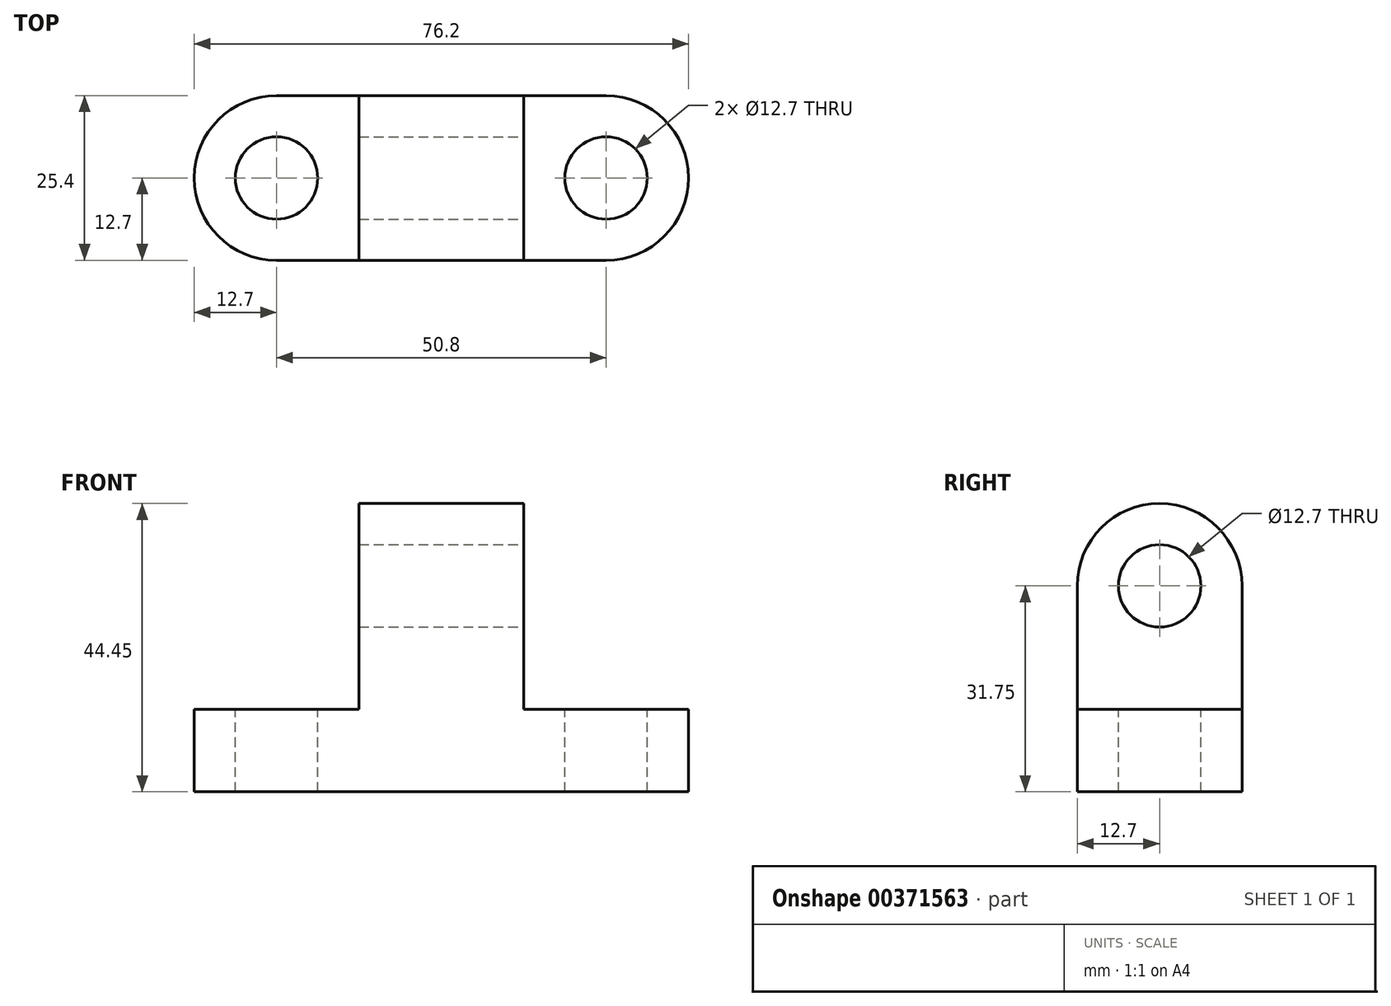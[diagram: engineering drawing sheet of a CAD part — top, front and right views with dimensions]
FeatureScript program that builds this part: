
annotation { "Feature Type Name" : "Feature", "Feature Type Description" : "" }
export const myFeature = defineFeature(function(context is Context, id is Id, definition is map)
    precondition{}
    {
        {
            var Q0;
            Q0=qCreatedBy(makeId("Front.planeOp"),FACE);
            var sketch = newSketch(context, id + "F0", { "sketchPlane" : qUnion([Q0])});
            skLineSegment(sketch, "E0", {"start": v(0, 0) * mm, "end": v(76.2, 0) * mm});
            skLineSegment(sketch, "E1", {"start": v(76.2, 0) * mm, "end": v(76.2, 12.7) * mm});
            skLineSegment(sketch, "E2", {"start": v(76.2, 12.7) * mm, "end": v(50.8, 12.7) * mm});
            skLineSegment(sketch, "E3", {"start": v(50.8, 12.7) * mm, "end": v(50.8, 44.45) * mm});
            skLineSegment(sketch, "E4", {"start": v(50.8, 44.45) * mm, "end": v(25.4, 44.45) * mm});
            skLineSegment(sketch, "E5", {"start": v(25.4, 44.45) * mm, "end": v(25.4, 12.7) * mm});
            skLineSegment(sketch, "E6", {"start": v(25.4, 12.7) * mm, "end": v(0, 12.7) * mm});
            skLineSegment(sketch, "E7", {"start": v(0, 12.7) * mm, "end": v(0, 0) * mm});
            skSolve(sketch);
        }
        {
            var Q0;
            Q0=makeQuery(id+"F0.imprint","IMPRINT",FACE,{"disambiguationData":[TD([[makeQuery(id+"F0.imprint","IMPRINT",EDGE,{"derivedFrom":sQuery(id+"F0.wireOp",EDGE,"E0")}),1.0]])]});
            extrude(context, id + "F1", {"entities" : qUnion([Q0]), "depth" : 25.4 * mm});
        }
        {
            var Q0;
            Q0=makeQuery(id+"F1.opExtrude","SWEPT_FACE",FACE,{"disambiguationData":[OSD([sQuery(id+"F0.wireOp",EDGE,"E3")])]});
            var sketch = newSketch(context, id + "F2", { "sketchPlane" : qUnion([Q0])});
            skCircle(sketch, "E8", {"center": v(-12.7, 31.75) * mm, "radius": 6.35 * mm});
            skPoint(sketch, "E8.centerSnap0", {"position": v(-12.7, 44.45) * mm});
            skArc(sketch, "E9", {"start": v(0, 31.75) * mm, "mid": v(-12.7, 44.45) * mm, "end": v(-25.4, 31.75) * mm});
            skSolve(sketch);
        }
        {
            var Q0;
            {var subQ0=sQuery(id+"F2.wireOp",EDGE,"E9");var subQ1=sQuery(id+"F0.wireOp",EDGE,"E3");var subQ2=makeQuery(id+"F1.opExtrude","CAP_EDGE",EDGE,{"disambiguationData":[OSD([subQ1])],"isStart":false});var subQ3=makeQuery(id+"F2.imprint","INTERSECT",VERTEX,{"derivedFrom":[subQ2,subQ0]});Q0=makeQuery(id+"F2.imprint","IMPRINT",FACE,{"disambiguationData":[TD([[makeQuery(id+"F2.imprint","IMPRINT",EDGE,{"disambiguationData":[TD([[subQ3,1.0]])],"derivedFrom":subQ0}),-1.0]])]});}
            var Q1;
            {var subQ0=sQuery(id+"F2.wireOp",EDGE,"E9");var subQ1=sQuery(id+"F0.wireOp",EDGE,"E3");var subQ2=makeQuery(id+"F1.opExtrude","CAP_EDGE",EDGE,{"disambiguationData":[OSD([subQ1])],"isStart":true});var subQ3=makeQuery(id+"F2.imprint","INTERSECT",VERTEX,{"derivedFrom":[subQ2,subQ0]});Q1=makeQuery(id+"F2.imprint","IMPRINT",FACE,{"disambiguationData":[TD([[makeQuery(id+"F2.imprint","IMPRINT",EDGE,{"disambiguationData":[TD([[subQ3,-1.0]])],"derivedFrom":subQ0}),-1.0]])]});}
            var Q2;
            Q2=makeQuery(id+"F2.imprint","IMPRINT",FACE,{"disambiguationData":[TD([[makeQuery(id+"F2.imprint","IMPRINT",EDGE,{"derivedFrom":sQuery(id+"F2.wireOp",EDGE,"E8")}),1.0]])]});
            extrude(context, id + "F3", {"entities" : qUnion([Q0, Q1, Q2]), "operationType" : NewBodyOperationType.REMOVE, "oppositeDirection" : true, "depth" : 25.4 * mm});
        }
        {
            var Q0;
            Q0=makeQuery(id+"F1.opExtrude","SWEPT_FACE",FACE,{"disambiguationData":[OSD([sQuery(id+"F0.wireOp",EDGE,"E6")])]});
            var sketch = newSketch(context, id + "F4", { "sketchPlane" : qUnion([Q0])});
            skCircle(sketch, "E10", {"center": v(12.7, -12.7) * mm, "radius": 6.35 * mm});
            skPoint(sketch, "E10.centerSnap0", {"position": v(0, -12.7) * mm});
            skArc(sketch, "E11", {"start": v(12.7, 0) * mm, "mid": v(0, -12.7) * mm, "end": v(12.7, -25.4) * mm});
            skSolve(sketch);
        }
        {
            var Q0;
            {var subQ0=sQuery(id+"F4.wireOp",EDGE,"E11");var subQ1=sQuery(id+"F0.wireOp",EDGE,"E6");var subQ2=makeQuery(id+"F1.opExtrude","CAP_EDGE",EDGE,{"disambiguationData":[OSD([subQ1])],"isStart":true});var subQ3=makeQuery(id+"F4.imprint","INTERSECT",VERTEX,{"derivedFrom":[subQ2,subQ0]});Q0=makeQuery(id+"F4.imprint","IMPRINT",FACE,{"disambiguationData":[TD([[makeQuery(id+"F4.imprint","IMPRINT",EDGE,{"disambiguationData":[TD([[subQ3,-1.0]])],"derivedFrom":subQ0}),-1.0]])]});}
            var Q1;
            Q1=makeQuery(id+"F4.imprint","IMPRINT",FACE,{"disambiguationData":[TD([[makeQuery(id+"F4.imprint","IMPRINT",EDGE,{"derivedFrom":sQuery(id+"F4.wireOp",EDGE,"E10")}),1.0]])]});
            var Q2;
            {var subQ0=sQuery(id+"F4.wireOp",EDGE,"E11");var subQ1=sQuery(id+"F0.wireOp",EDGE,"E6");var subQ2=makeQuery(id+"F1.opExtrude","CAP_EDGE",EDGE,{"disambiguationData":[OSD([subQ1])],"isStart":false});var subQ3=makeQuery(id+"F4.imprint","INTERSECT",VERTEX,{"derivedFrom":[subQ2,subQ0]});Q2=makeQuery(id+"F4.imprint","IMPRINT",FACE,{"disambiguationData":[TD([[makeQuery(id+"F4.imprint","IMPRINT",EDGE,{"disambiguationData":[TD([[subQ3,1.0]])],"derivedFrom":subQ0}),-1.0]])]});}
            extrude(context, id + "F5", {"entities" : qUnion([Q0, Q1, Q2]), "operationType" : NewBodyOperationType.REMOVE, "oppositeDirection" : true, "depth" : 25.4 * mm});
        }
        {
            var Q0;
            Q0=makeQuery(id+"F1.opExtrude","SWEPT_FACE",FACE,{"disambiguationData":[OSD([sQuery(id+"F0.wireOp",EDGE,"E2")])]});
            var sketch = newSketch(context, id + "F6", { "sketchPlane" : qUnion([Q0])});
            skCircle(sketch, "E12", {"center": v(63.5, -12.7) * mm, "radius": 6.35 * mm});
            skPoint(sketch, "E12.centerSnap0", {"position": v(76.2, -12.7) * mm});
            skArc(sketch, "E13", {"start": v(63.5, -25.4) * mm, "mid": v(76.2, -12.7) * mm, "end": v(63.5, 0) * mm});
            skSolve(sketch);
        }
        {
            var Q0;
            {var subQ0=sQuery(id+"F6.wireOp",EDGE,"E13");var subQ1=sQuery(id+"F0.wireOp",EDGE,"E2");var subQ2=makeQuery(id+"F1.opExtrude","CAP_EDGE",EDGE,{"disambiguationData":[OSD([subQ1])],"isStart":true});var subQ3=makeQuery(id+"F6.imprint","INTERSECT",VERTEX,{"derivedFrom":[subQ2,subQ0]});Q0=makeQuery(id+"F6.imprint","IMPRINT",FACE,{"disambiguationData":[TD([[makeQuery(id+"F6.imprint","IMPRINT",EDGE,{"disambiguationData":[TD([[subQ3,1.0]])],"derivedFrom":subQ0}),-1.0]])]});}
            var Q1;
            {var subQ0=sQuery(id+"F6.wireOp",EDGE,"E13");var subQ1=sQuery(id+"F0.wireOp",EDGE,"E2");var subQ2=makeQuery(id+"F1.opExtrude","CAP_EDGE",EDGE,{"disambiguationData":[OSD([subQ1])],"isStart":false});var subQ3=makeQuery(id+"F6.imprint","INTERSECT",VERTEX,{"derivedFrom":[subQ2,subQ0]});Q1=makeQuery(id+"F6.imprint","IMPRINT",FACE,{"disambiguationData":[TD([[makeQuery(id+"F6.imprint","IMPRINT",EDGE,{"disambiguationData":[TD([[subQ3,-1.0]])],"derivedFrom":subQ0}),-1.0]])]});}
            var Q2;
            Q2=makeQuery(id+"F6.imprint","IMPRINT",FACE,{"disambiguationData":[TD([[makeQuery(id+"F6.imprint","IMPRINT",EDGE,{"derivedFrom":sQuery(id+"F6.wireOp",EDGE,"E12")}),1.0]])]});
            extrude(context, id + "F7", {"entities" : qUnion([Q0, Q1, Q2]), "operationType" : NewBodyOperationType.REMOVE, "oppositeDirection" : true, "depth" : 25.4 * mm});
        }
    });
